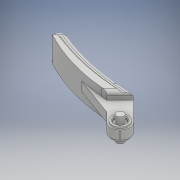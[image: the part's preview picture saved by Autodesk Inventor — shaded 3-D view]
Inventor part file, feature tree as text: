
AUTODESK INVENTOR PART (.ipt)
format: ipt  version: 2018 (Build 220112000, 112)  size: 484,352 bytes
history: native  units: mm
features: extrude x7, sketch x7, projected_geometry x5, other x2, fillet x2, chamfer x1
ambient origin geometry x8: Origin, YZ Plane, XZ Plane, XY Plane, X Axis, Y Axis, Z Axis, Center Point
bodies: Body1 (feature_tree)
feature tree (24):
  other  "ソリッド2"
  extrude  "押し出し1"  Depth=10.0mm TaperAngle=0.0deg
  extrude  "押し出し2"  Depth=5.0mm
  fillet  "フィレット1"  Radius=20.0mm
  extrude  "押し出し3"  Depth=2.0mm
  extrude  "押し出し4"  Depth=4.0mm
  fillet  "フィレット2"  Radius=5.0mm
  extrude  "押し出し5"  Depth=4.0mm TaperAngle=0.0deg
  extrude  "押し出し6"  Depth=4.0mm TaperAngle=0.0deg
  extrude  "押し出し7"  Depth=5.0mm
  chamfer  "面取り1"  Distance=8.0mm
  sketch  "スケッチ1"
  sketch  "スケッチ2"
  sketch  "スケッチ3"
  sketch  "スケッチ4"
  sketch  "スケッチ6"
  projected_geometry  "投影ループ3"
  projected_geometry  "投影ループ4"
  projected_geometry  "投影ループ5"
  sketch  "スケッチ7"
  projected_geometry  "投影ループ6"
  sketch  "スケッチ8"
  projected_geometry  "投影ループ7"
  other  "ソリッド1"
